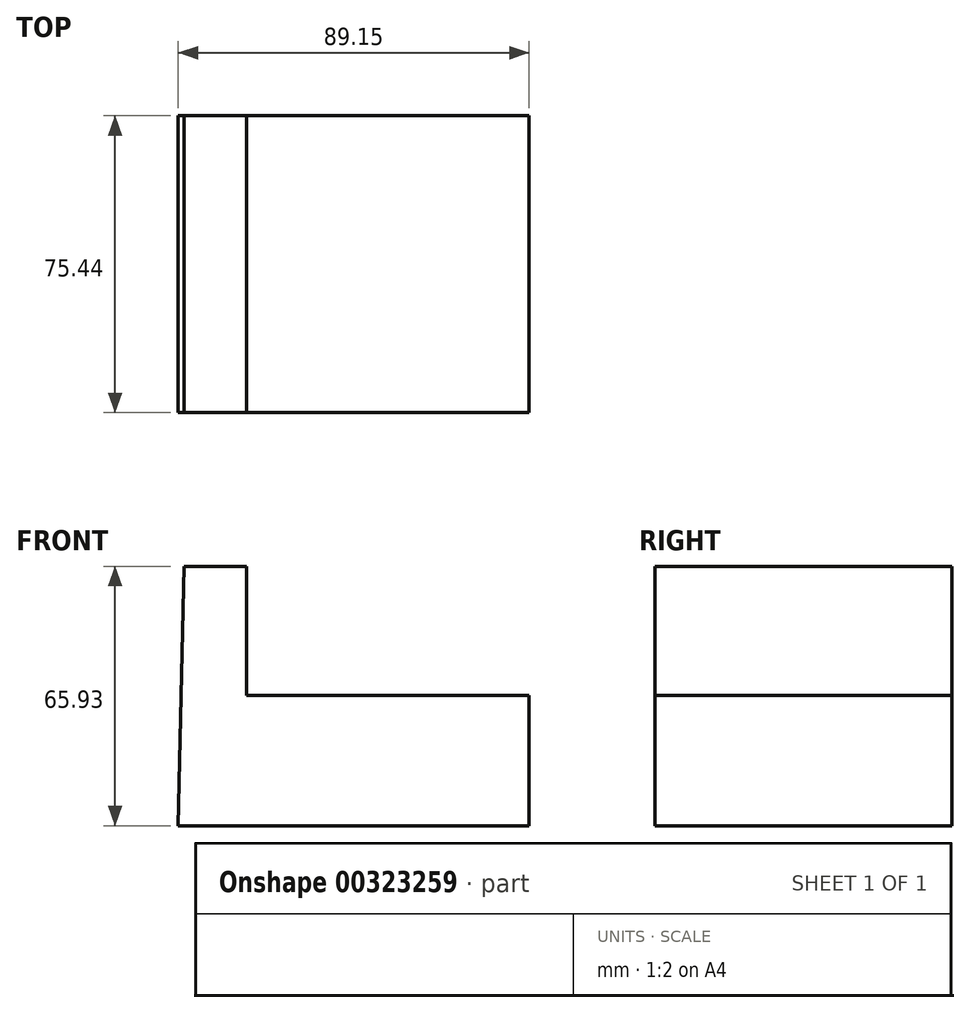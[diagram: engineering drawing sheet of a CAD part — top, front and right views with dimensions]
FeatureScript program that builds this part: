
annotation { "Feature Type Name" : "Feature", "Feature Type Description" : "" }
export const myFeature = defineFeature(function(context is Context, id is Id, definition is map)
    precondition{}
    {
        {
            var Q0;
            Q0=qCreatedBy(makeId("Front.planeOp"),FACE);
            var sketch = newSketch(context, id + "F0", { "sketchPlane" : qUnion([Q0])});
            skLineSegment(sketch, "E0", {"start": v(-46.12, 48.44) * mm, "end": v(41.48, 48.44) * mm});
            skLineSegment(sketch, "E1", {"start": v(41.48, 48.44) * mm, "end": v(41.48, -17.49) * mm});
            skLineSegment(sketch, "E2", {"start": v(41.48, -17.49) * mm, "end": v(-47.67, -17.49) * mm});
            skLineSegment(sketch, "E3", {"start": v(-47.67, -17.49) * mm, "end": v(-46.12, 48.44) * mm});
            skSolve(sketch);
        }
        {
            var Q0;
            Q0=makeQuery(id+"F0.imprint","IMPRINT",FACE,{"disambiguationData":[TD([[makeQuery(id+"F0.imprint","IMPRINT",EDGE,{"derivedFrom":sQuery(id+"F0.wireOp",EDGE,"E0")}),-1.0]])]});
            extrude(context, id + "F1", {"entities" : qUnion([Q0]), "depth" : 75.44 * mm});
        }
        {
            var Q0;
            Q0=qCreatedBy(makeId("Front.planeOp"),FACE);
            var sketch = newSketch(context, id + "F2", { "sketchPlane" : qUnion([Q0])});
            skLineSegment(sketch, "E4", {"start": v(-30.33, 48.44) * mm, "end": v(33.74, 48.44) * mm});
            skLineSegment(sketch, "E5", {"start": v(-30.33, 48.44) * mm, "end": v(-30.33, 15.63) * mm});
            skLineSegment(sketch, "E6", {"start": v(42.1, 15.63) * mm, "end": v(42.1, 48.44) * mm});
            skLineSegment(sketch, "E7", {"start": v(42.1, 48.44) * mm, "end": v(42.1, 15.63) * mm});
            skLineSegment(sketch, "E8", {"start": v(-30.33, 15.63) * mm, "end": v(42.1, 15.63) * mm});
            skLineSegment(sketch, "E9", {"start": v(33.74, 48.44) * mm, "end": v(42.1, 48.44) * mm});
            skSolve(sketch);
        }
        {
            var Q0;
            Q0=makeQuery(id+"F2.imprint","IMPRINT",FACE,{"disambiguationData":[TD([[makeQuery(id+"F2.imprint","IMPRINT",EDGE,{"derivedFrom":sQuery(id+"F2.wireOp",EDGE,"E4")}),-1.0]])]});
            extrude(context, id + "F3", {"entities" : qUnion([Q0]), "operationType" : NewBodyOperationType.REMOVE, "depth" : 95.76 * mm});
        }
    });
